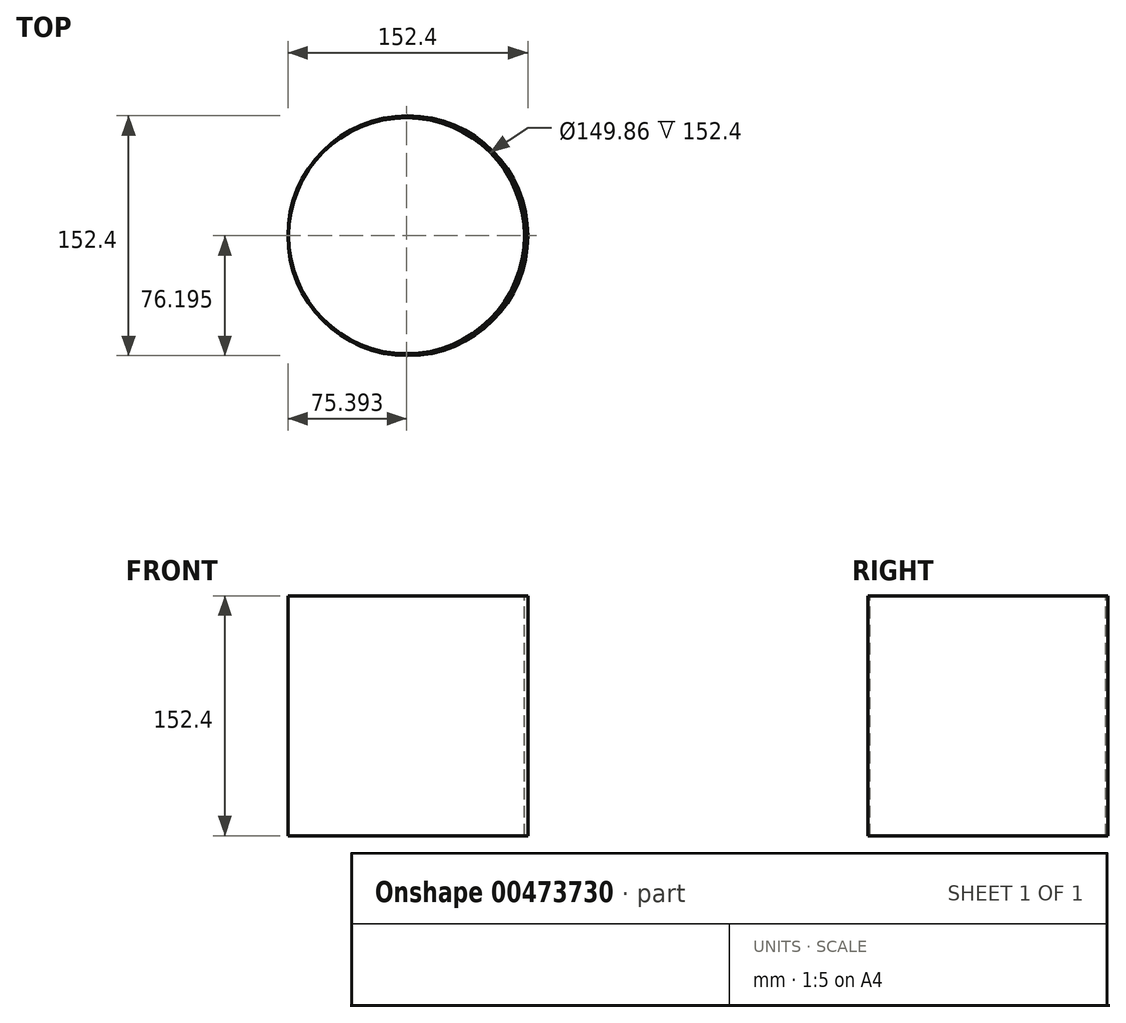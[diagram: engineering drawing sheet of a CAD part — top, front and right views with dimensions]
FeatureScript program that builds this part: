
annotation { "Feature Type Name" : "Feature", "Feature Type Description" : "" }
export const myFeature = defineFeature(function(context is Context, id is Id, definition is map)
    precondition{}
    {
        {
            var Q0;
            Q0=qCreatedBy(makeId("Top.planeOp"),FACE);
            var sketch = newSketch(context, id + "F0", { "sketchPlane" : qUnion([Q0])});
            skCircle(sketch, "E0", {"center": v(-66.9, -11.3) * mm, "radius": 76.2 * mm});
            skSolve(sketch);
        }
        {
            var Q0;
            Q0=makeQuery(id+"F0.imprint","IMPRINT",FACE,{"disambiguationData":[TD([[makeQuery(id+"F0.imprint","IMPRINT",EDGE,{"derivedFrom":sQuery(id+"F0.wireOp",EDGE,"E0")}),1.0]])]});
            extrude(context, id + "F1", {"entities" : qUnion([Q0]), "depth" : 152.4 * mm});
        }
        {
            var Q0;
            Q0=makeQuery(id+"F1.opExtrude","CAP_FACE",FACE,{"disambiguationData":[OSD([sQuery(id+"F0.wireOp",EDGE,"E0")])],"isStart":false});
            var sketch = newSketch(context, id + "F2", { "sketchPlane" : qUnion([Q0])});
            skLineSegment(sketch, "E1", {"start": v(-67.72, -87.5) * mm, "end": v(-67.72, 64.9) * mm});
            skCircle(sketch, "E2", {"center": v(-67.72, -11.3) * mm, "radius": 74.93 * mm});
            skSolve(sketch);
        }
        {
            var Q0;
            {var subQ0=sQuery(id+"F2.wireOp",EDGE,"E2");var subQ1=sQuery(id+"F2.wireOp",EDGE,"E1");var subQ2=makeQuery(id+"F2.imprint","INTERSECT",VERTEX,{"disambiguationData":[OD(0.0)],"derivedFrom":[subQ1,subQ0]});Q0=makeQuery(id+"F2.imprint","IMPRINT",FACE,{"disambiguationData":[TD([[makeQuery(id+"F2.imprint","IMPRINT",EDGE,{"disambiguationData":[TD([[subQ2,-1.0]])],"derivedFrom":subQ1}),1.0]])]});}
            var Q1;
            {var subQ0=sQuery(id+"F2.wireOp",EDGE,"E2");var subQ1=sQuery(id+"F2.wireOp",EDGE,"E1");var subQ2=makeQuery(id+"F2.imprint","INTERSECT",VERTEX,{"disambiguationData":[OD(0.0)],"derivedFrom":[subQ1,subQ0]});Q1=makeQuery(id+"F2.imprint","IMPRINT",FACE,{"disambiguationData":[TD([[makeQuery(id+"F2.imprint","IMPRINT",EDGE,{"disambiguationData":[TD([[subQ2,-1.0]])],"derivedFrom":subQ1}),-1.0]])]});}
            extrude(context, id + "F3", {"entities" : qUnion([Q0, Q1]), "operationType" : NewBodyOperationType.REMOVE, "oppositeDirection" : true, "depth" : 152.4 * mm});
        }
    });
